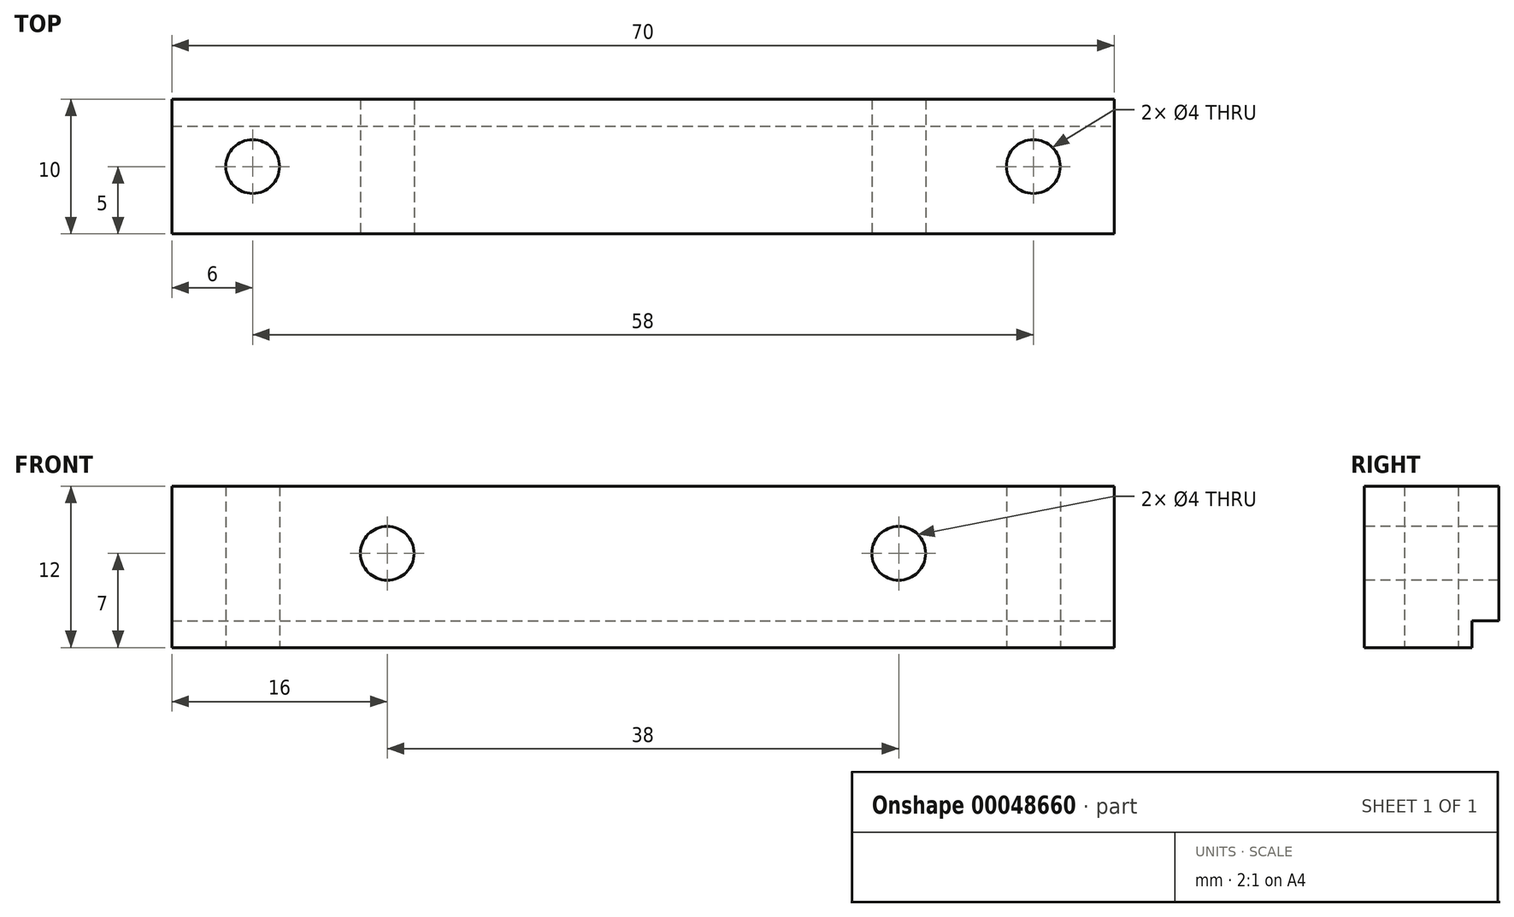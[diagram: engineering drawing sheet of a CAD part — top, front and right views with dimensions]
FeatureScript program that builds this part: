
annotation { "Feature Type Name" : "Feature", "Feature Type Description" : "" }
export const myFeature = defineFeature(function(context is Context, id is Id, definition is map)
    precondition{}
    {
        {
            var Q0;
            Q0=qCreatedBy(makeId("Top.planeOp"),FACE);
            var sketch = newSketch(context, id + "F0", { "sketchPlane" : qUnion([Q0])});
            skLineSegment(sketch, "E0.bottom", {"start": v(0, 0) * mm, "end": v(70, 0) * mm});
            skLineSegment(sketch, "E0.top", {"start": v(0, -10) * mm, "end": v(70, -10) * mm});
            skLineSegment(sketch, "E0.left", {"start": v(0, 0) * mm, "end": v(0, -10) * mm});
            skLineSegment(sketch, "E0.right", {"start": v(70, 0) * mm, "end": v(70, -10) * mm});
            skCircle(sketch, "E1", {"center": v(6, -5) * mm, "radius": 2 * mm});
            skCircle(sketch, "E2", {"center": v(64, -5) * mm, "radius": 2 * mm});
            skSolve(sketch);
        }
        {
            var Q0;
            Q0 = qSketchRegion(id + "F0", true);
            extrude(context, id + "F1", {"entities" : qUnion([Q0]), "depth" : 12 * mm});
        }
        {
            var Q0;
            Q0=qCreatedBy(makeId("Top.planeOp"),FACE);
            var sketch = newSketch(context, id + "F2", { "sketchPlane" : qUnion([Q0])});
            skLineSegment(sketch, "E3.bottom", {"start": v(0, 0) * mm, "end": v(70, 0) * mm});
            skLineSegment(sketch, "E3.top", {"start": v(0, -2) * mm, "end": v(70, -2) * mm});
            skLineSegment(sketch, "E3.left", {"start": v(0, 0) * mm, "end": v(0, -2) * mm});
            skLineSegment(sketch, "E3.right", {"start": v(70, 0) * mm, "end": v(70, -2) * mm});
            skSolve(sketch);
        }
        {
            var Q0;
            Q0 = qSketchRegion(id + "F2", true);
            extrude(context, id + "F3", {"entities" : qUnion([Q0]), "operationType" : NewBodyOperationType.REMOVE, "depth" : 2 * mm});
        }
        {
            var Q0;
            Q0=makeQuery(id+"F1.opExtrude","SWEPT_FACE",FACE,{"disambiguationData":[OSD([sQuery(id+"F0.wireOp",EDGE,"E0.top")])]});
            var sketch = newSketch(context, id + "F4", { "sketchPlane" : qUnion([Q0])});
            skCircle(sketch, "E4", {"center": v(16, 7) * mm, "radius": 2 * mm});
            skCircle(sketch, "E5", {"center": v(54, 7) * mm, "radius": 2 * mm});
            skSolve(sketch);
        }
        {
            var Q0;
            Q0 = qSketchRegion(id + "F4", true);
            extrude(context, id + "F5", {"entities" : qUnion([Q0]), "operationType" : NewBodyOperationType.REMOVE, "oppositeDirection" : true, "depth" : 25 * mm});
        }
    });
